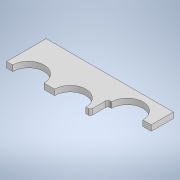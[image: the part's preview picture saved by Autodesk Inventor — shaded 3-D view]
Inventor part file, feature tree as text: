
AUTODESK INVENTOR PART (.ipt)
format: ipt  version: 2021 (Build 250183000, 183)  size: 156,160 bytes
history: native  units: mm
features: extrude x2, sketch x2, projected_geometry x1
ambient origin geometry x8: Origin, YZ Plane, XZ Plane, XY Plane, X Axis, Y Axis, Z Axis, Center Point
bodies: Solid1 (feature_tree)
feature tree (5):
  extrude  "Extrusion1"  Depth=35.0mm
  extrude  "Extrusion2"  Depth=19.5mm
  sketch  "Sketch1"  dims[d0=47.7mm d1=27.7mm d2=27.7mm d3=27.7mm d4=27.7mm d7=37.0mm d9=30.9mm d10=19.5mm d11=35.0mm d12=35.0mm d13=25.8mm d14=28.0mm d15=56.25mm]
  sketch  "Sketch2"  dims[d16=58.25mm d17=116.5mm d18=112.5mm d19=18.5mm d20=32.45mm d21=5.0mm d22=0.0mm d23=74.0mm d25=38.5mm d26=2.0mm d27=35.0mm d28=19.5mm d29=0.0mm d30=0.0mm d31=27.0mm d32=9.60644mm d33=27.0mm d34=7.944139mm]
  projected_geometry  "Projected Loop1"
